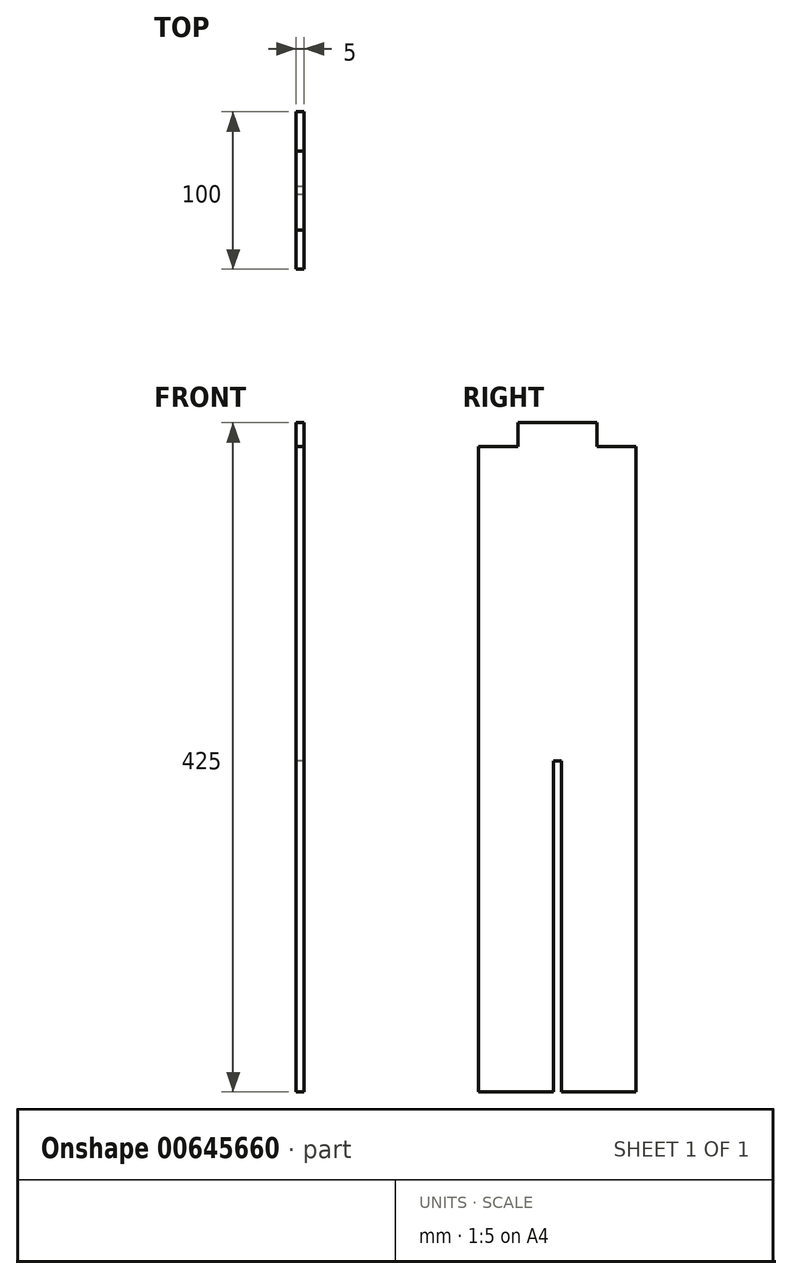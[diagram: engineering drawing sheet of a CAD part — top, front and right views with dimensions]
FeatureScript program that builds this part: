
annotation { "Feature Type Name" : "Feature", "Feature Type Description" : "" }
export const myFeature = defineFeature(function(context is Context, id is Id, definition is map)
    precondition{}
    {
        {
            var Q0;
            Q0=qCreatedBy(makeId("Right.planeOp"),FACE);
            var sketch = newSketch(context, id + "F0", { "sketchPlane" : qUnion([Q0])});
            skLineSegment(sketch, "E0.top", {"start": v(0, 410) * mm, "end": v(-25, 410) * mm});
            skLineSegment(sketch, "E0.left", {"start": v(0, 0) * mm, "end": v(0, 410) * mm});
            skLineSegment(sketch, "E0.right", {"start": v(-100, 0) * mm, "end": v(-100, 410) * mm});
            skLineSegment(sketch, "E1.top", {"start": v(-75, 425) * mm, "end": v(-25, 425) * mm});
            skLineSegment(sketch, "E1.left", {"start": v(-75, 410) * mm, "end": v(-75, 425) * mm});
            skLineSegment(sketch, "E1.right", {"start": v(-25, 410) * mm, "end": v(-25, 425) * mm});
            skLineSegment(sketch, "E2", {"start": v(-100, 0) * mm, "end": v(-52.5, 0) * mm});
            skLineSegment(sketch, "E3.trimOffspring", {"start": v(-75, 410) * mm, "end": v(-100, 410) * mm});
            skPoint(sketch, "E4.oppositeSnap0", {"position": v(-50, 0) * mm});
            skLineSegment(sketch, "E4.bottom", {"start": v(-50, 0) * mm, "end": v(-50, 0) * mm});
            skLineSegment(sketch, "E5.top", {"start": v(-52.5, 210) * mm, "end": v(-47.5, 210) * mm});
            skLineSegment(sketch, "E5.left", {"start": v(-52.5, 0) * mm, "end": v(-52.5, 210) * mm});
            skLineSegment(sketch, "E5.right", {"start": v(-47.5, 0) * mm, "end": v(-47.5, 210) * mm});
            skLineSegment(sketch, "E6.trimOffspring", {"start": v(-47.5, 0) * mm, "end": v(0, 0) * mm});
            skSolve(sketch);
        }
        {
            var Q0;
            Q0=makeQuery(id+"F0.imprint","IMPRINT",FACE,{"disambiguationData":[TD([[makeQuery(id+"F0.imprint","IMPRINT",EDGE,{"derivedFrom":sQuery(id+"F0.wireOp",EDGE,"E0.top")}),1.0]])]});
            extrude(context, id + "F1", {"entities" : qUnion([Q0]), "depth" : 5 * mm, "offsetDistance" : 25 * mm});
        }
    });
